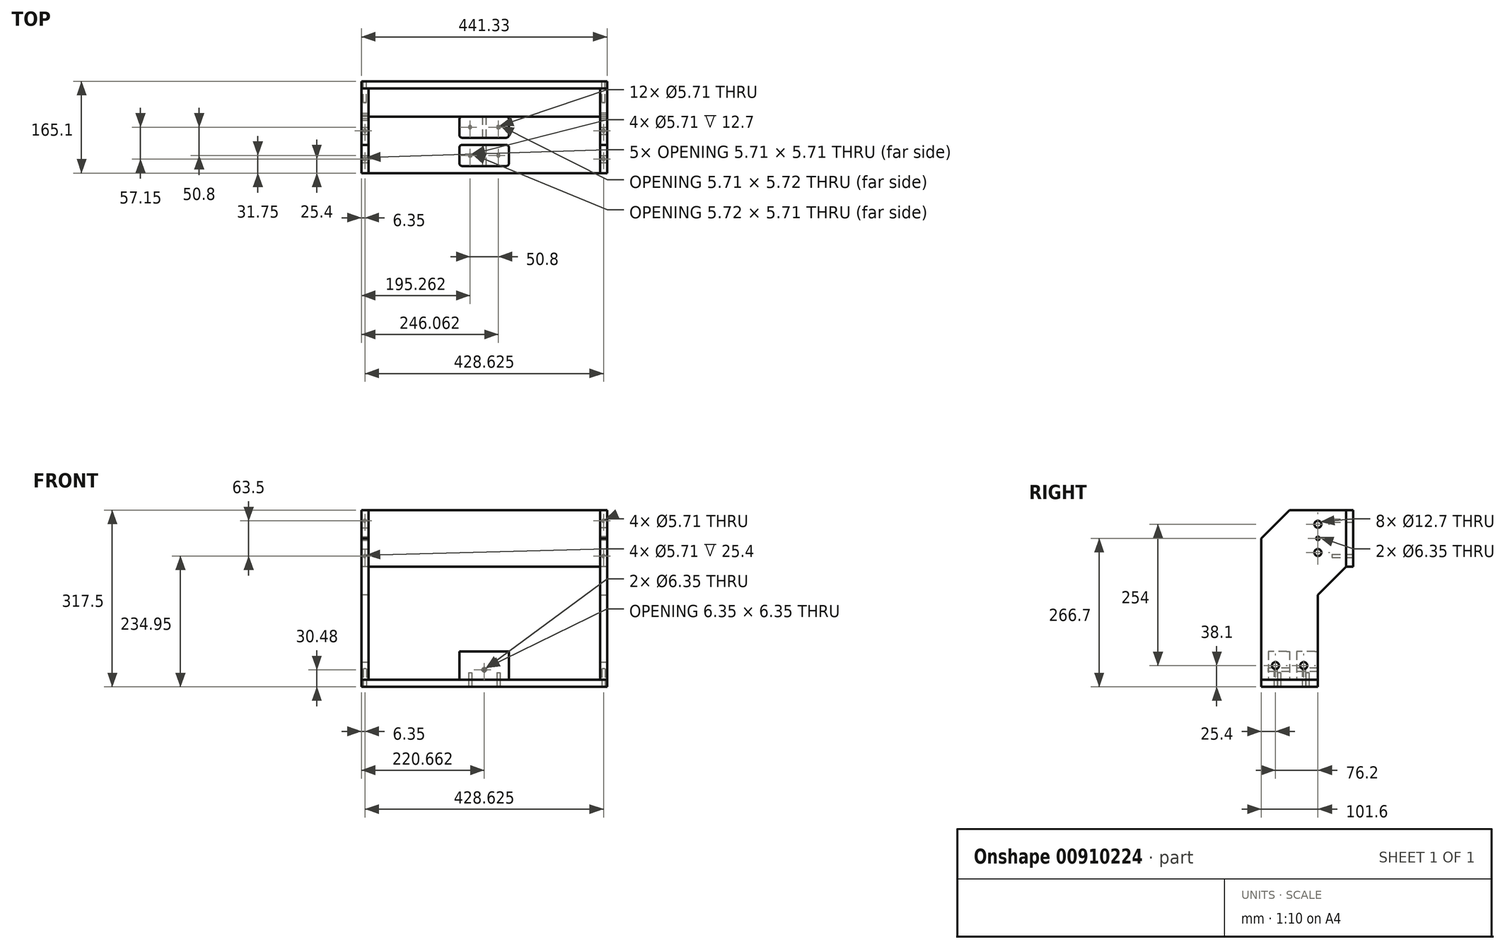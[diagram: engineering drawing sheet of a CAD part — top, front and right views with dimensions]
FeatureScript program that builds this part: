
annotation { "Feature Type Name" : "Feature", "Feature Type Description" : "" }
export const myFeature = defineFeature(function(context is Context, id is Id, definition is map)
    precondition{}
    {
        {
            var Q0;
            Q0=qCreatedBy(makeId("Right.planeOp"),FACE);
            var sketch = newSketch(context, id + "F0", { "sketchPlane" : qUnion([Q0])});
            skLineSegment(sketch, "E0.bottom", {"start": v(-50.8, 152.4) * mm, "end": v(50.8, 152.4) * mm});
            skLineSegment(sketch, "E0.top", {"start": v(-50.8, -152.4) * mm, "end": v(50.8, -152.4) * mm});
            skLineSegment(sketch, "E0.left", {"start": v(-50.8, 152.4) * mm, "end": v(-50.8, -152.4) * mm});
            skLineSegment(sketch, "E0.right", {"start": v(50.8, 152.4) * mm, "end": v(50.8, -152.4) * mm});
            skPoint(sketch, "E0.middle", {"position": v(0, 0) * mm});
            skLineSegment(sketch, "E1.bottom", {"start": v(-50.8, 152.4) * mm, "end": v(101.6, 152.4) * mm});
            skLineSegment(sketch, "E1.top", {"start": v(-50.8, 50.8) * mm, "end": v(101.6, 50.8) * mm});
            skLineSegment(sketch, "E1.left", {"start": v(-50.8, 152.4) * mm, "end": v(-50.8, 50.8) * mm});
            skLineSegment(sketch, "E1.right", {"start": v(101.6, 152.4) * mm, "end": v(101.6, 50.8) * mm});
            skPoint(sketch, "E2.end.orphan", {"position": v(25.4, 152.4) * mm});
            skLineSegment(sketch, "E3", {"start": v(101.6, 50.8) * mm, "end": v(50.8, 0) * mm});
            skPoint(sketch, "E4.start.orphan", {"position": v(50.8, 0) * mm});
            skLineSegment(sketch, "E5", {"start": v(0, 152.4) * mm, "end": v(-50.8, 101.6) * mm});
            skSolve(sketch);
        }
        {
            var Q0;
            {var subQ1=sQuery(id+"F0.wireOp",EDGE,"E0.top");Q0=makeQuery(id+"F0.imprint","IMPRINT",FACE,{"disambiguationData":[TD([[makeQuery(id+"F0.imprint","IMPRINT",EDGE,{"derivedFrom":subQ1}),1.0]])]});}
            var Q1;
            {var subQ5=sQuery(id+"F0.wireOp",EDGE,"E1.right");Q1=makeQuery(id+"F0.imprint","IMPRINT",FACE,{"disambiguationData":[TD([[makeQuery(id+"F0.imprint","IMPRINT",EDGE,{"derivedFrom":subQ5}),-1.0]])]});}
            var Q2;
            {var subQ0=sQuery(id+"F0.wireOp",EDGE,"E4");Q2=makeQuery(id+"F0.imprint","IMPRINT",FACE,{"disambiguationData":[TD([[makeQuery(id+"F0.imprint","IMPRINT",EDGE,{"derivedFrom":subQ0}),1.0]])]});}
            var Q3;
            {var subQ5=sQuery(id+"F0.wireOp",EDGE,"E2");Q3=makeQuery(id+"F0.imprint","IMPRINT",FACE,{"disambiguationData":[TD([[makeQuery(id+"F0.imprint","IMPRINT",EDGE,{"derivedFrom":subQ5}),-1.0]])]});}
            var Q4;
            {var subQ5=sQuery(id+"F0.wireOp",EDGE,"E5");Q4=makeQuery(id+"F0.imprint","IMPRINT",FACE,{"disambiguationData":[TD([[makeQuery(id+"F0.imprint","IMPRINT",EDGE,{"derivedFrom":subQ5}),1.0]])]});}
            var Q5;
            {var subQ0=sQuery(id+"F0.wireOp",EDGE,"E3");Q5=makeQuery(id+"F0.imprint","IMPRINT",FACE,{"disambiguationData":[TD([[makeQuery(id+"F0.imprint","IMPRINT",EDGE,{"derivedFrom":subQ0}),-1.0]])]});}
            extrude(context, id + "F1", {"entities" : qUnion([Q0, Q1, Q2, Q3, Q4, Q5]), "depth" : 12.7 * mm, "offsetDistance" : 25.4 * mm});
        }
        {
            var Q0;
            Q0=qCreatedBy(makeId("Right.planeOp"),FACE);
            var sketch = newSketch(context, id + "F2", { "sketchPlane" : qUnion([Q0])});
            skLineSegment(sketch, "E6.bottom", {"start": v(-50.8, -152.4) * mm, "end": v(50.8, -152.4) * mm});
            skLineSegment(sketch, "E6.top", {"start": v(-50.8, -165.1) * mm, "end": v(50.8, -165.1) * mm});
            skLineSegment(sketch, "E6.left", {"start": v(-50.8, -152.4) * mm, "end": v(-50.8, -165.1) * mm});
            skLineSegment(sketch, "E6.right", {"start": v(50.8, -152.4) * mm, "end": v(50.8, -165.1) * mm});
            skSolve(sketch);
        }
        {
            var Q0;
            Q0 = qSketchRegion(id + "F2", true);
            extrude(context, id + "F3", {"entities" : qUnion([Q0]), "depth" : 441.32 * mm, "offsetDistance" : 25.4 * mm});
        }
        {
            var Q0;
            Q0=makeQuery(id+"F1.opExtrude","CAP_FACE",FACE,{"disambiguationData":[OSD([sQuery(id+"F0.wireOp",EDGE,"E0.top"),sQuery(id+"F0.wireOp",EDGE,"E0.left"),sQuery(id+"F0.wireOp",EDGE,"E0.right"),sQuery(id+"F0.wireOp",EDGE,"E1.bottom"),sQuery(id+"F0.wireOp",EDGE,"E1.left"),sQuery(id+"F0.wireOp",EDGE,"E1.right"),sQuery(id+"F0.wireOp",EDGE,"E3"),sQuery(id+"F0.wireOp",EDGE,"E5")])],"isStart":false});
            var sketch = newSketch(context, id + "F4", { "sketchPlane" : qUnion([Q0])});
            skLineSegment(sketch, "E7.bottom", {"start": v(0, 152.4) * mm, "end": v(101.6, 152.4) * mm, "construction": true});
            skLineSegment(sketch, "E7.top", {"start": v(0, 50.8) * mm, "end": v(101.6, 50.8) * mm, "construction": true});
            skLineSegment(sketch, "E7.left", {"start": v(0, 152.4) * mm, "end": v(0, 50.8) * mm, "construction": true});
            skLineSegment(sketch, "E7.right", {"start": v(101.6, 152.4) * mm, "end": v(101.6, 50.8) * mm, "construction": true});
            skLineSegment(sketch, "E8", {"start": v(50.8, 152.4) * mm, "end": v(50.8, 50.8) * mm, "construction": true});
            skPoint(sketch, "E9", {"position": v(50.8, 101.6) * mm});
            skLineSegment(sketch, "E10", {"start": v(50.8, 101.6) * mm, "end": v(50.8, 152.4) * mm, "construction": true});
            skPoint(sketch, "E11", {"position": v(50.8, 127) * mm});
            skLineSegment(sketch, "E12", {"start": v(50.8, 101.6) * mm, "end": v(50.8, 50.8) * mm, "construction": true});
            skPoint(sketch, "E13", {"position": v(50.8, 76.2) * mm});
            skCircle(sketch, "E14", {"center": v(50.8, 127) * mm, "radius": 6.35 * mm});
            skCircle(sketch, "E15", {"center": v(50.8, 76.2) * mm, "radius": 6.35 * mm});
            skCircle(sketch, "E16", {"center": v(50.8, 101.6) * mm, "radius": 3.18 * mm});
            skSolve(sketch);
        }
        {
            var Q0;
            Q0=makeQuery(id+"F4.imprint","IMPRINT",FACE,{"disambiguationData":[TD([[makeQuery(id+"F4.imprint","IMPRINT",EDGE,{"derivedFrom":sQuery(id+"F4.wireOp",EDGE,"E14")}),1.0]])]});
            var Q1;
            Q1=makeQuery(id+"F4.imprint","IMPRINT",FACE,{"disambiguationData":[TD([[makeQuery(id+"F4.imprint","IMPRINT",EDGE,{"derivedFrom":sQuery(id+"F4.wireOp",EDGE,"E16")}),1.0]])]});
            var Q2;
            Q2=makeQuery(id+"F4.imprint","IMPRINT",FACE,{"disambiguationData":[TD([[makeQuery(id+"F4.imprint","IMPRINT",EDGE,{"derivedFrom":sQuery(id+"F4.wireOp",EDGE,"E15")}),1.0]])]});
            extrude(context, id + "F5", {"entities" : qUnion([Q0, Q1, Q2]), "operationType" : NewBodyOperationType.REMOVE, "oppositeDirection" : true, "depth" : 25.4 * mm, "offsetDistance" : 25.4 * mm});
        }
        {
            var Q0;
            Q0=qCreatedBy(makeId("Right.planeOp"),FACE);
            cPlane(context, id + "F6", {"entities" : qUnion([Q0]), "cplaneType" : CPlaneType.OFFSET, "offset" : 220.66 * mm, "width" : 152.4 * mm, "height" : 152.4 * mm});
        }
        {
            var Q0;
            Q0=makeQuery(id+"F1.opExtrude","SWEPT_BODY",BODY,{"disambiguationData":[OSD([sQuery(id+"F0.wireOp",EDGE,"E0.top"),sQuery(id+"F0.wireOp",EDGE,"E0.left"),sQuery(id+"F0.wireOp",EDGE,"E0.right"),sQuery(id+"F0.wireOp",EDGE,"E1.bottom"),sQuery(id+"F0.wireOp",EDGE,"E1.right"),sQuery(id+"F0.wireOp",EDGE,"E4"),sQuery(id+"F0.wireOp",EDGE,"E2")])]});
            var Q1;
            Q1=qCreatedBy(id+"F6.planeOp",FACE);
            mirror(context, id + "F7", {"entities" : qUnion([Q0]), "mirrorPlane" : qUnion([Q1])});
        }
        {
            var Q0;
            Q0=qCreatedBy(makeId("Right.planeOp"),FACE);
            var sketch = newSketch(context, id + "F8", { "sketchPlane" : qUnion([Q0])});
            skPoint(sketch, "E17.bottom.start.orphan", {"position": v(101.6, 152.4) * mm});
            skLineSegment(sketch, "E18.bottom", {"start": v(101.6, 152.4) * mm, "end": v(114.3, 152.4) * mm});
            skLineSegment(sketch, "E18.top", {"start": v(101.6, 50.8) * mm, "end": v(114.3, 50.8) * mm});
            skLineSegment(sketch, "E18.left", {"start": v(101.6, 152.4) * mm, "end": v(101.6, 50.8) * mm});
            skLineSegment(sketch, "E18.right", {"start": v(114.3, 152.4) * mm, "end": v(114.3, 50.8) * mm});
            skSolve(sketch);
        }
        {
            var Q0;
            Q0 = qSketchRegion(id + "F8", true);
            extrude(context, id + "F9", {"entities" : qUnion([Q0]), "depth" : 441.32 * mm, "offsetDistance" : 25.4 * mm});
        }
        {
            var Q0;
            Q0=makeQuery(id+"F7.opPattern","COPY",FACE,{"derivedFrom":makeQuery(id+"F1.opExtrude","CAP_FACE",FACE,{"disambiguationData":[OSD([sQuery(id+"F0.wireOp",EDGE,"E0.top"),sQuery(id+"F0.wireOp",EDGE,"E0.left"),sQuery(id+"F0.wireOp",EDGE,"E0.right"),sQuery(id+"F0.wireOp",EDGE,"E1.bottom"),sQuery(id+"F0.wireOp",EDGE,"E1.right"),sQuery(id+"F0.wireOp",EDGE,"E4"),sQuery(id+"F0.wireOp",EDGE,"E2")])],"isStart":true}),"instanceName":"1"});
            var sketch = newSketch(context, id + "F10", { "sketchPlane" : qUnion([Q0])});
            skLineSegment(sketch, "E19.bottom", {"start": v(-50.8, -152.4) * mm, "end": v(50.8, -152.4) * mm, "construction": true});
            skLineSegment(sketch, "E19.top", {"start": v(-50.8, -127) * mm, "end": v(50.8, -127) * mm, "construction": true});
            skLineSegment(sketch, "E19.left", {"start": v(-50.8, -152.4) * mm, "end": v(-50.8, -127) * mm, "construction": true});
            skLineSegment(sketch, "E19.right", {"start": v(50.8, -152.4) * mm, "end": v(50.8, -127) * mm, "construction": true});
            skCircle(sketch, "E20", {"center": v(-25.4, -127) * mm, "radius": 6.35 * mm});
            skCircle(sketch, "E21", {"center": v(25.4, -127) * mm, "radius": 6.35 * mm});
            skLineSegment(sketch, "E22", {"start": v(-50.8, -127) * mm, "end": v(-25.4, -127) * mm});
            skLineSegment(sketch, "E23", {"start": v(-25.4, -127) * mm, "end": v(25.4, -127) * mm});
            skLineSegment(sketch, "E24", {"start": v(25.4, -127) * mm, "end": v(50.8, -127) * mm});
            skSolve(sketch);
        }
        {
            var Q0;
            Q0 = qSketchRegion(id + "F10", true);
            extrude(context, id + "F11", {"entities" : qUnion([Q0]), "operationType" : NewBodyOperationType.REMOVE, "oppositeDirection" : true, "depth" : 508 * mm, "offsetDistance" : 25.4 * mm});
        }
        {
            var Q0;
            Q0=makeQuery(id+"F3.opExtrude","SWEPT_FACE",FACE,{"disambiguationData":[OSD([sQuery(id+"F2.wireOp",EDGE,"E6.bottom")])]});
            var sketch = newSketch(context, id + "F12", { "sketchPlane" : qUnion([Q0])});
            skLineSegment(sketch, "E25", {"start": v(220.66, 50.8) * mm, "end": v(220.66, -19.05) * mm, "construction": true});
            skLineSegment(sketch, "E26.bottom", {"start": v(176.21, 0) * mm, "end": v(265.11, 0) * mm});
            skLineSegment(sketch, "E26.top", {"start": v(176.21, -38.1) * mm, "end": v(265.11, -38.1) * mm});
            skLineSegment(sketch, "E26.left", {"start": v(176.21, 0) * mm, "end": v(176.21, -38.1) * mm});
            skLineSegment(sketch, "E26.right", {"start": v(265.11, 0) * mm, "end": v(265.11, -38.1) * mm});
            skPoint(sketch, "E26.middle", {"position": v(220.66, -19.05) * mm});
            skLineSegment(sketch, "E27.bottom", {"start": v(176.21, 50.8) * mm, "end": v(265.11, 50.8) * mm});
            skLineSegment(sketch, "E27.top", {"start": v(176.21, 12.7) * mm, "end": v(265.11, 12.7) * mm});
            skLineSegment(sketch, "E27.left", {"start": v(176.21, 50.8) * mm, "end": v(176.21, 12.7) * mm});
            skLineSegment(sketch, "E27.right", {"start": v(265.11, 50.8) * mm, "end": v(265.11, 12.7) * mm});
            skPoint(sketch, "E27.middle", {"position": v(220.66, 31.75) * mm});
            skSolve(sketch);
        }
        {
            var Q0;
            Q0 = qSketchRegion(id + "F12", true);
            extrude(context, id + "F13", {"entities" : qUnion([Q0]), "depth" : 50.8 * mm, "offsetDistance" : 25.4 * mm});
        }
        {
            var Q0;
            Q0=makeQuery(id+"F13.opExtrude","SWEPT_EDGE",EDGE,{"disambiguationData":[OSD([sQuery(id+"F12.wireOp",EDGE,"E26.top"),sQuery(id+"F12.wireOp",EDGE,"E26.left")])]});
            var Q1;
            Q1=makeQuery(id+"F13.opExtrude","SWEPT_EDGE",EDGE,{"disambiguationData":[OSD([sQuery(id+"F12.wireOp",EDGE,"E26.bottom"),sQuery(id+"F12.wireOp",EDGE,"E26.left")])]});
            var Q2;
            Q2=makeQuery(id+"F13.opExtrude","SWEPT_EDGE",EDGE,{"disambiguationData":[OSD([sQuery(id+"F12.wireOp",EDGE,"E27.top"),sQuery(id+"F12.wireOp",EDGE,"E27.left")])]});
            var Q3;
            Q3=makeQuery(id+"F13.opExtrude","SWEPT_EDGE",EDGE,{"disambiguationData":[OSD([sQuery(id+"F2.wireOp",EDGE,"E6.bottom"),sQuery(id+"F2.wireOp",EDGE,"E6.right"),sQuery(id+"F12.wireOp",EDGE,"E27.bottom"),sQuery(id+"F12.wireOp",EDGE,"E27.left")])]});
            var Q4;
            Q4=makeQuery(id+"F13.opExtrude","SWEPT_EDGE",EDGE,{"disambiguationData":[OSD([sQuery(id+"F12.wireOp",EDGE,"E26.top"),sQuery(id+"F12.wireOp",EDGE,"E26.right")])]});
            var Q5;
            Q5=makeQuery(id+"F13.opExtrude","SWEPT_EDGE",EDGE,{"disambiguationData":[OSD([sQuery(id+"F12.wireOp",EDGE,"E26.bottom"),sQuery(id+"F12.wireOp",EDGE,"E26.right")])]});
            var Q6;
            Q6=makeQuery(id+"F13.opExtrude","SWEPT_EDGE",EDGE,{"disambiguationData":[OSD([sQuery(id+"F12.wireOp",EDGE,"E27.top"),sQuery(id+"F12.wireOp",EDGE,"E27.right")])]});
            var Q7;
            Q7=makeQuery(id+"F13.opExtrude","SWEPT_EDGE",EDGE,{"disambiguationData":[OSD([sQuery(id+"F2.wireOp",EDGE,"E6.bottom"),sQuery(id+"F2.wireOp",EDGE,"E6.right"),sQuery(id+"F12.wireOp",EDGE,"E27.bottom"),sQuery(id+"F12.wireOp",EDGE,"E27.right")])]});
            fillet(context, id + "F14", {"entities" : qUnion([Q0, Q1, Q2, Q3, Q4, Q5, Q6, Q7]), "radius" : 5.08 * mm, "tangentPropagation" : true, "allowEdgeOverflow" : false});
        }
        {
            var Q0;
            Q0=makeQuery(id+"F3.opExtrude","SWEPT_FACE",FACE,{"disambiguationData":[OSD([sQuery(id+"F2.wireOp",EDGE,"E6.top")])]});
            var sketch = newSketch(context, id + "F15", { "sketchPlane" : qUnion([Q0])});
            skCircle(sketch, "E28", {"center": v(195.26, 19.05) * mm, "radius": 2.86 * mm});
            skCircle(sketch, "E29", {"center": v(246.06, 19.05) * mm, "radius": 2.86 * mm});
            skCircle(sketch, "E30", {"center": v(195.26, -31.75) * mm, "radius": 2.86 * mm});
            skCircle(sketch, "E31", {"center": v(246.06, -31.75) * mm, "radius": 2.86 * mm});
            skLineSegment(sketch, "E32.bottom", {"start": v(195.26, 19.05) * mm, "end": v(246.06, 19.05) * mm, "construction": true});
            skLineSegment(sketch, "E32.top", {"start": v(195.26, -31.75) * mm, "end": v(246.06, -31.75) * mm, "construction": true});
            skLineSegment(sketch, "E32.left", {"start": v(195.26, 19.05) * mm, "end": v(195.26, -31.75) * mm, "construction": true});
            skLineSegment(sketch, "E32.right", {"start": v(246.06, 19.05) * mm, "end": v(246.06, -31.75) * mm, "construction": true});
            skLineSegment(sketch, "E33", {"start": v(220.66, 19.05) * mm, "end": v(220.66, 38.1) * mm, "construction": true});
            skSolve(sketch);
        }
        {
            var Q0;
            Q0 = qSketchRegion(id + "F15", true);
            extrude(context, id + "F16", {"entities" : qUnion([Q0]), "operationType" : NewBodyOperationType.REMOVE, "oppositeDirection" : true, "depth" : 25.4 * mm, "offsetDistance" : 25.4 * mm});
        }
        {
            var Q0;
            Q0=makeQuery(id+"F13.opExtrude","SWEPT_FACE",FACE,{"disambiguationData":[OSD([sQuery(id+"F12.wireOp",EDGE,"E26.top")])]});
            var sketch = newSketch(context, id + "F17", { "sketchPlane" : qUnion([Q0])});
            skCircle(sketch, "E34", {"center": v(220.66, -134.62) * mm, "radius": 3.17 * mm});
            skLineSegment(sketch, "E35", {"start": v(220.66, -134.62) * mm, "end": v(220.66, -152.4) * mm, "construction": true});
            skSolve(sketch);
        }
        {
            var Q0;
            Q0 = qSketchRegion(id + "F17", true);
            extrude(context, id + "F18", {"entities" : qUnion([Q0]), "operationType" : NewBodyOperationType.REMOVE, "oppositeDirection" : true, "depth" : 101.6 * mm, "offsetDistance" : 25.4 * mm});
        }
        {
            var Q0;
            Q0=makeQuery(id+"F9.opExtrude","SWEPT_FACE",FACE,{"disambiguationData":[OSD([sQuery(id+"F8.wireOp",EDGE,"E18.right")])]});
            var sketch = newSketch(context, id + "F19", { "sketchPlane" : qUnion([Q0])});
            skLineSegment(sketch, "E36.bottom", {"start": v(-434.98, 133.35) * mm, "end": v(-6.35, 133.35) * mm, "construction": true});
            skLineSegment(sketch, "E36.top", {"start": v(-434.98, 69.85) * mm, "end": v(-6.35, 69.85) * mm, "construction": true});
            skLineSegment(sketch, "E36.left", {"start": v(-434.98, 133.35) * mm, "end": v(-434.98, 69.85) * mm, "construction": true});
            skLineSegment(sketch, "E36.right", {"start": v(-6.35, 133.35) * mm, "end": v(-6.35, 69.85) * mm, "construction": true});
            skCircle(sketch, "E37", {"center": v(-6.35, 133.35) * mm, "radius": 2.86 * mm});
            skCircle(sketch, "E38", {"center": v(-6.35, 69.85) * mm, "radius": 2.86 * mm});
            skCircle(sketch, "E39", {"center": v(-434.98, 133.35) * mm, "radius": 2.86 * mm});
            skCircle(sketch, "E40", {"center": v(-434.98, 69.85) * mm, "radius": 2.86 * mm});
            skSolve(sketch);
        }
        {
            var Q0;
            Q0 = qSketchRegion(id + "F19", true);
            extrude(context, id + "F20", {"entities" : qUnion([Q0]), "operationType" : NewBodyOperationType.REMOVE, "oppositeDirection" : true, "depth" : 38.1 * mm, "offsetDistance" : 25.4 * mm});
        }
        {
            var Q0;
            Q0=makeQuery(id+"F3.opExtrude","SWEPT_FACE",FACE,{"disambiguationData":[OSD([sQuery(id+"F2.wireOp",EDGE,"E6.top")])]});
            var sketch = newSketch(context, id + "F21", { "sketchPlane" : qUnion([Q0])});
            skLineSegment(sketch, "E41.0", {"start": v(434.98, 44.45) * mm, "end": v(6.35, 44.45) * mm});
            skLineSegment(sketch, "E41.1", {"start": v(434.98, 44.45) * mm, "end": v(434.98, -44.45) * mm});
            skLineSegment(sketch, "E41.2", {"start": v(434.98, -44.45) * mm, "end": v(6.35, -44.45) * mm});
            skLineSegment(sketch, "E41.3", {"start": v(6.35, 44.45) * mm, "end": v(6.35, -44.45) * mm});
            skCircle(sketch, "E42", {"center": v(6.35, 25.4) * mm, "radius": 2.86 * mm});
            skCircle(sketch, "E43", {"center": v(6.35, -25.4) * mm, "radius": 2.86 * mm});
            skCircle(sketch, "E44", {"center": v(434.98, 25.4) * mm, "radius": 2.86 * mm});
            skCircle(sketch, "E45", {"center": v(434.98, -25.4) * mm, "radius": 2.86 * mm});
            skSolve(sketch);
        }
        {
            var Q0;
            Q0=makeQuery(id+"F21.imprint","IMPRINT",FACE,{"disambiguationData":[TD([[makeQuery(id+"F21.imprint","IMPRINT",EDGE,{"derivedFrom":makeQuery(id+"F16.boolean.opBoolean","COPY",EDGE,{"derivedFrom":makeQuery(id+"F16.opExtrude","CAP_EDGE",EDGE,{"disambiguationData":[OSD([sQuery(id+"F15.wireOp",EDGE,"E28")])],"isStart":true})})}),1.0]])]});
            var Q1;
            Q1=makeQuery(id+"F21.imprint","IMPRINT",FACE,{"disambiguationData":[TD([[makeQuery(id+"F21.imprint","IMPRINT",EDGE,{"derivedFrom":makeQuery(id+"F16.boolean.opBoolean","COPY",EDGE,{"derivedFrom":makeQuery(id+"F16.opExtrude","CAP_EDGE",EDGE,{"disambiguationData":[OSD([sQuery(id+"F15.wireOp",EDGE,"E29")])],"isStart":true})})}),1.0]])]});
            var Q2;
            Q2=makeQuery(id+"F21.imprint","IMPRINT",FACE,{"disambiguationData":[TD([[makeQuery(id+"F21.imprint","IMPRINT",EDGE,{"derivedFrom":makeQuery(id+"F16.boolean.opBoolean","COPY",EDGE,{"derivedFrom":makeQuery(id+"F16.opExtrude","CAP_EDGE",EDGE,{"disambiguationData":[OSD([sQuery(id+"F15.wireOp",EDGE,"E30")])],"isStart":true})})}),1.0]])]});
            var Q3;
            Q3=makeQuery(id+"F21.imprint","IMPRINT",FACE,{"disambiguationData":[TD([[makeQuery(id+"F21.imprint","IMPRINT",EDGE,{"derivedFrom":makeQuery(id+"F16.boolean.opBoolean","COPY",EDGE,{"derivedFrom":makeQuery(id+"F16.opExtrude","CAP_EDGE",EDGE,{"disambiguationData":[OSD([sQuery(id+"F15.wireOp",EDGE,"E31")])],"isStart":true})})}),1.0]])]});
            var Q4;
            {var subQ0=sQuery(id+"F21.wireOp",EDGE,"E44");var subQ1=sQuery(id+"F21.wireOp",EDGE,"E41.1");var subQ2=makeQuery(id+"F21.imprint","INTERSECT",VERTEX,{"disambiguationData":[OD(0.0)],"derivedFrom":[subQ1,subQ0]});Q4=makeQuery(id+"F21.imprint","IMPRINT",FACE,{"disambiguationData":[TD([[makeQuery(id+"F21.imprint","IMPRINT",EDGE,{"disambiguationData":[TD([[subQ2,-1.0]])],"derivedFrom":subQ1}),-1.0]])]});}
            var Q5;
            {var subQ0=sQuery(id+"F21.wireOp",EDGE,"E44");var subQ1=sQuery(id+"F21.wireOp",EDGE,"E41.1");var subQ2=makeQuery(id+"F21.imprint","INTERSECT",VERTEX,{"disambiguationData":[OD(0.0)],"derivedFrom":[subQ1,subQ0]});Q5=makeQuery(id+"F21.imprint","IMPRINT",FACE,{"disambiguationData":[TD([[makeQuery(id+"F21.imprint","IMPRINT",EDGE,{"disambiguationData":[TD([[subQ2,-1.0]])],"derivedFrom":subQ1}),1.0]])]});}
            var Q6;
            {var subQ0=sQuery(id+"F21.wireOp",EDGE,"E45");var subQ1=sQuery(id+"F21.wireOp",EDGE,"E41.1");var subQ2=makeQuery(id+"F21.imprint","INTERSECT",VERTEX,{"disambiguationData":[OD(0.0)],"derivedFrom":[subQ1,subQ0]});Q6=makeQuery(id+"F21.imprint","IMPRINT",FACE,{"disambiguationData":[TD([[makeQuery(id+"F21.imprint","IMPRINT",EDGE,{"disambiguationData":[TD([[subQ2,-1.0]])],"derivedFrom":subQ1}),-1.0]])]});}
            var Q7;
            {var subQ0=sQuery(id+"F21.wireOp",EDGE,"E45");var subQ1=sQuery(id+"F21.wireOp",EDGE,"E41.1");var subQ2=makeQuery(id+"F21.imprint","INTERSECT",VERTEX,{"disambiguationData":[OD(0.0)],"derivedFrom":[subQ1,subQ0]});Q7=makeQuery(id+"F21.imprint","IMPRINT",FACE,{"disambiguationData":[TD([[makeQuery(id+"F21.imprint","IMPRINT",EDGE,{"disambiguationData":[TD([[subQ2,-1.0]])],"derivedFrom":subQ1}),1.0]])]});}
            var Q8;
            {var subQ0=sQuery(id+"F21.wireOp",EDGE,"E43");var subQ1=sQuery(id+"F21.wireOp",EDGE,"E41.3");var subQ2=makeQuery(id+"F21.imprint","INTERSECT",VERTEX,{"disambiguationData":[OD(0.0)],"derivedFrom":[subQ1,subQ0]});Q8=makeQuery(id+"F21.imprint","IMPRINT",FACE,{"disambiguationData":[TD([[makeQuery(id+"F21.imprint","IMPRINT",EDGE,{"disambiguationData":[TD([[subQ2,-1.0]])],"derivedFrom":subQ1}),-1.0]])]});}
            var Q9;
            {var subQ0=sQuery(id+"F21.wireOp",EDGE,"E43");var subQ1=sQuery(id+"F21.wireOp",EDGE,"E41.3");var subQ2=makeQuery(id+"F21.imprint","INTERSECT",VERTEX,{"disambiguationData":[OD(0.0)],"derivedFrom":[subQ1,subQ0]});Q9=makeQuery(id+"F21.imprint","IMPRINT",FACE,{"disambiguationData":[TD([[makeQuery(id+"F21.imprint","IMPRINT",EDGE,{"disambiguationData":[TD([[subQ2,-1.0]])],"derivedFrom":subQ1}),1.0]])]});}
            var Q10;
            {var subQ0=sQuery(id+"F21.wireOp",EDGE,"E42");var subQ1=sQuery(id+"F21.wireOp",EDGE,"E41.3");var subQ2=makeQuery(id+"F21.imprint","INTERSECT",VERTEX,{"disambiguationData":[OD(0.0)],"derivedFrom":[subQ1,subQ0]});Q10=makeQuery(id+"F21.imprint","IMPRINT",FACE,{"disambiguationData":[TD([[makeQuery(id+"F21.imprint","IMPRINT",EDGE,{"disambiguationData":[TD([[subQ2,-1.0]])],"derivedFrom":subQ1}),-1.0]])]});}
            var Q11;
            {var subQ0=sQuery(id+"F21.wireOp",EDGE,"E42");var subQ1=sQuery(id+"F21.wireOp",EDGE,"E41.3");var subQ2=makeQuery(id+"F21.imprint","INTERSECT",VERTEX,{"disambiguationData":[OD(0.0)],"derivedFrom":[subQ1,subQ0]});Q11=makeQuery(id+"F21.imprint","IMPRINT",FACE,{"disambiguationData":[TD([[makeQuery(id+"F21.imprint","IMPRINT",EDGE,{"disambiguationData":[TD([[subQ2,-1.0]])],"derivedFrom":subQ1}),1.0]])]});}
            extrude(context, id + "F22", {"entities" : qUnion([Q0, Q1, Q2, Q3, Q4, Q5, Q6, Q7, Q8, Q9, Q10, Q11]), "operationType" : NewBodyOperationType.REMOVE, "oppositeDirection" : true, "depth" : 38.1 * mm, "offsetDistance" : 25.4 * mm});
        }
    });
